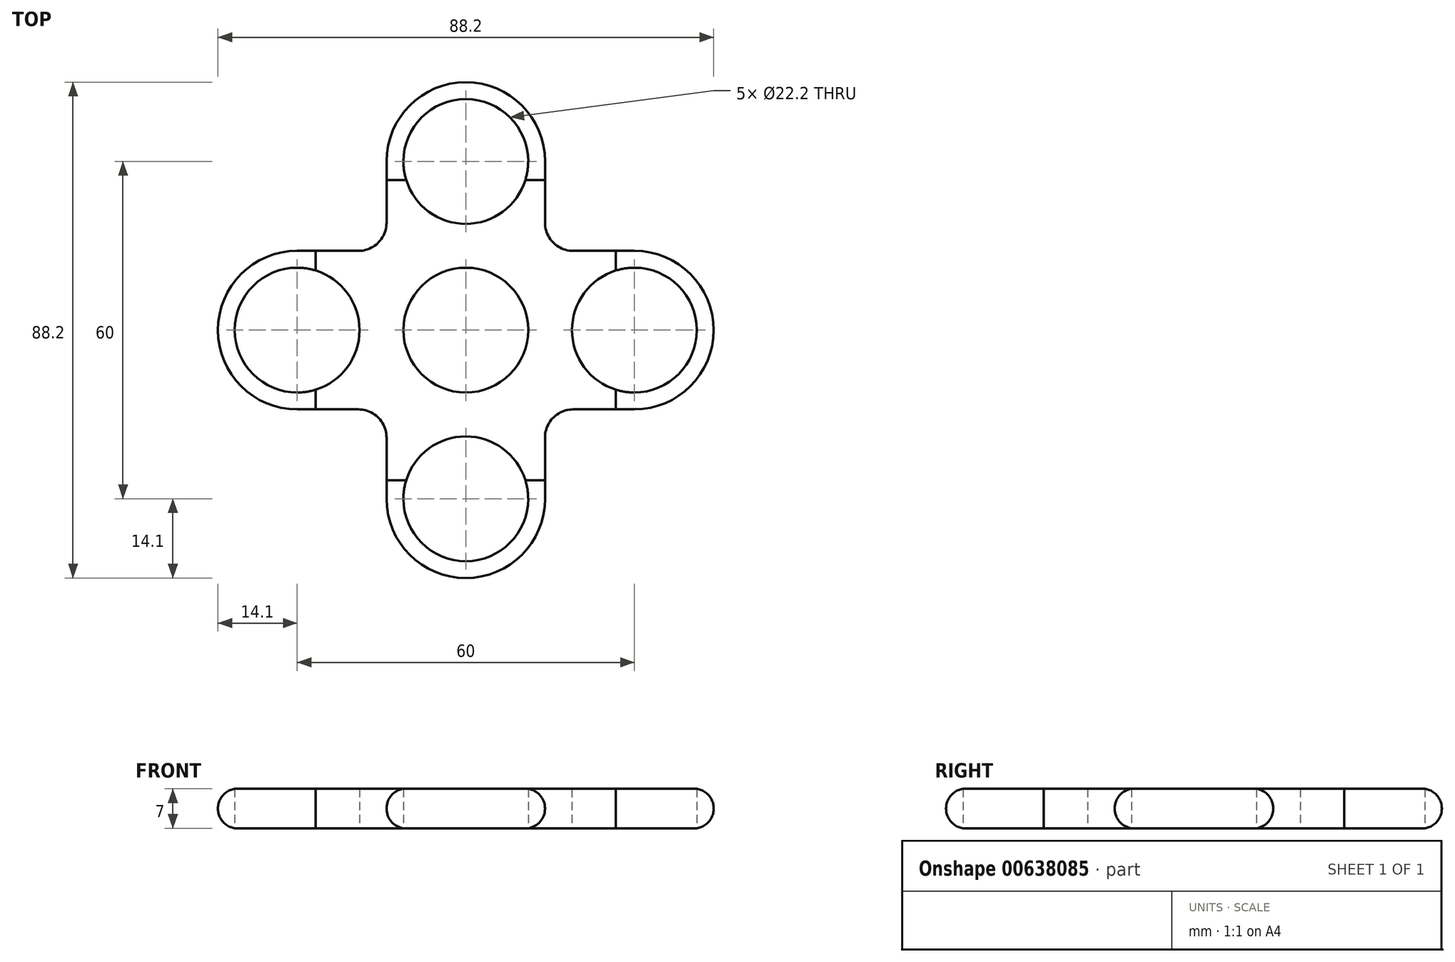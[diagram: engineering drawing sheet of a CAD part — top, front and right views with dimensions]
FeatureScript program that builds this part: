
annotation { "Feature Type Name" : "Feature", "Feature Type Description" : "" }
export const myFeature = defineFeature(function(context is Context, id is Id, definition is map)
    precondition{}
    {
        {
            var Q0;
            Q0=qCreatedBy(makeId("Top.planeOp"),FACE);
            var sketch = newSketch(context, id + "F0", { "sketchPlane" : qUnion([Q0])});
            skCircle(sketch, "E0", {"center": v(0, 0) * mm, "radius": 11.1 * mm});
            skCircle(sketch, "E1", {"center": v(0, 30) * mm, "radius": 11.1 * mm});
            skCircle(sketch, "E2.1.0", {"center": v(-30, 0) * mm, "radius": 11.1 * mm});
            skCircle(sketch, "E2.2.0", {"center": v(0, -30) * mm, "radius": 11.1 * mm});
            skCircle(sketch, "E2.3.0", {"center": v(30, 0) * mm, "radius": 11.1 * mm});
            skArc(sketch, "E3.0", {"start": v(14.1, 30) * mm, "mid": v(0, 44.1) * mm, "end": v(-14.1, 30) * mm});
            skLineSegment(sketch, "E4", {"start": v(14.1, 30) * mm, "end": v(14.1, 14.1) * mm});
            skLineSegment(sketch, "E5", {"start": v(-14.1, 30) * mm, "end": v(-14.1, 14.1) * mm});
            skLineSegment(sketch, "E6.1.0", {"start": v(-30, 14.1) * mm, "end": v(-14.1, 14.1) * mm});
            skLineSegment(sketch, "E6.1.1", {"start": v(-30, -14.1) * mm, "end": v(-14.1, -14.1) * mm});
            skArc(sketch, "E6.1.2", {"start": v(-30, 14.1) * mm, "mid": v(-44.1, 0) * mm, "end": v(-30, -14.1) * mm});
            skLineSegment(sketch, "E6.2.0", {"start": v(-14.1, -30) * mm, "end": v(-14.1, -14.1) * mm});
            skLineSegment(sketch, "E6.2.1", {"start": v(14.1, -30) * mm, "end": v(14.1, -14.1) * mm});
            skArc(sketch, "E6.2.2", {"start": v(-14.1, -30) * mm, "mid": v(0, -44.1) * mm, "end": v(14.1, -30) * mm});
            skLineSegment(sketch, "E6.3.0", {"start": v(30, -14.1) * mm, "end": v(14.1, -14.1) * mm});
            skLineSegment(sketch, "E6.3.1", {"start": v(30, 14.1) * mm, "end": v(14.1, 14.1) * mm});
            skArc(sketch, "E6.3.2", {"start": v(30, -14.1) * mm, "mid": v(44.1, 0) * mm, "end": v(30, 14.1) * mm});
            skPoint(sketch, "E7.orphan", {"position": v(14.1, 3.54) * mm});
            skPoint(sketch, "E8.orphan", {"position": v(-14.1, -2.74) * mm});
            skPoint(sketch, "E9.orphan", {"position": v(-3.54, 14.1) * mm});
            skPoint(sketch, "E10.orphan", {"position": v(-2.74, 14.1) * mm});
            skPoint(sketch, "E11.orphan", {"position": v(-14.1, -3.54) * mm});
            skPoint(sketch, "E12.orphan", {"position": v(14.1, 2.74) * mm});
            skPoint(sketch, "E13.orphan", {"position": v(3.54, -14.1) * mm});
            skPoint(sketch, "E14.orphan", {"position": v(2.74, -14.1) * mm});
            skPoint(sketch, "E15.start.orphan", {"position": v(-15.25, 30) * mm});
            skSolve(sketch);
        }
        {
            var Q0;
            Q0=makeQuery(id+"F0.imprint","IMPRINT",FACE,{"disambiguationData":[TD([[makeQuery(id+"F0.imprint","IMPRINT",EDGE,{"derivedFrom":sQuery(id+"F0.wireOp",EDGE,"E0")}),-1.0]])]});
            extrude(context, id + "F1", {"entities" : qUnion([Q0]), "depth" : 7 * mm, "offsetDistance" : 25 * mm});
        }
        {
            var Q0;
            Q0=makeQuery(id+"F1.opExtrude","SWEPT_EDGE",EDGE,{"disambiguationData":[OSD([sQuery(id+"F0.wireOp",EDGE,"E4"),sQuery(id+"F0.wireOp",EDGE,"E6.3.1")])]});
            var Q1;
            Q1=makeQuery(id+"F1.opExtrude","SWEPT_EDGE",EDGE,{"disambiguationData":[OSD([sQuery(id+"F0.wireOp",EDGE,"E5"),sQuery(id+"F0.wireOp",EDGE,"E6.1.0")])]});
            var Q2;
            Q2=makeQuery(id+"F1.opExtrude","SWEPT_EDGE",EDGE,{"disambiguationData":[OSD([sQuery(id+"F0.wireOp",EDGE,"E6.1.1"),sQuery(id+"F0.wireOp",EDGE,"E6.2.0")])]});
            var Q3;
            Q3=makeQuery(id+"F1.opExtrude","SWEPT_EDGE",EDGE,{"disambiguationData":[OSD([sQuery(id+"F0.wireOp",EDGE,"E6.2.1"),sQuery(id+"F0.wireOp",EDGE,"E6.3.0")])]});
            fillet(context, id + "F2", {"entities" : qUnion([Q0, Q1, Q2, Q3]), "radius" : 5 * mm, "tangentPropagation" : true, "allowEdgeOverflow" : false});
        }
        {
            var Q0;
            Q0=makeQuery(id+"F1.opExtrude","CAP_EDGE",EDGE,{"disambiguationData":[OSD([sQuery(id+"F0.wireOp",EDGE,"E6.3.0")])],"isStart":false});
            var Q1;
            Q1=makeQuery(id+"F1.opExtrude","CAP_EDGE",EDGE,{"disambiguationData":[OSD([sQuery(id+"F0.wireOp",EDGE,"E6.3.2")])],"isStart":true});
            fillet(context, id + "F3", {"entities" : qUnion([Q0, Q1]), "radius" : 3.5 * mm, "tangentPropagation" : true, "allowEdgeOverflow" : false});
        }
    });
